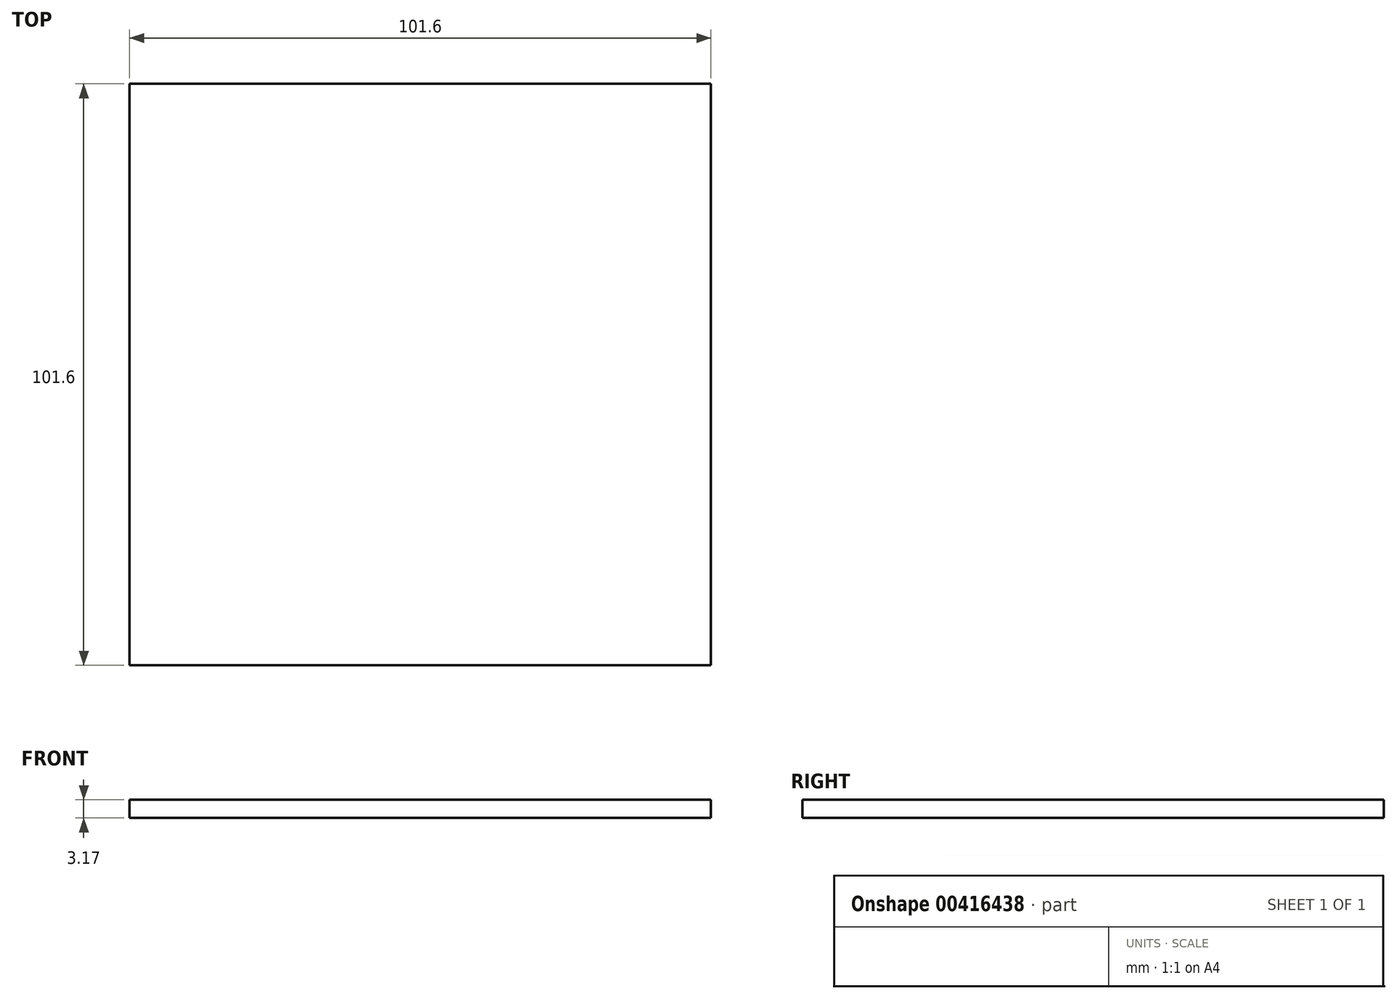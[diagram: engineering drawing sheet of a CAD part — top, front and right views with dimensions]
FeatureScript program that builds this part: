
annotation { "Feature Type Name" : "Feature", "Feature Type Description" : "" }
export const myFeature = defineFeature(function(context is Context, id is Id, definition is map)
    precondition{}
    {
        {
            var Q0;
            Q0=qCreatedBy(makeId("Top.planeOp"),FACE);
            var sketch = newSketch(context, id + "F0", { "sketchPlane" : qUnion([Q0])});
            skLineSegment(sketch, "E0.bottom", {"start": v(50.8, 50.8) * mm, "end": v(-50.8, 50.8) * mm});
            skLineSegment(sketch, "E0.top", {"start": v(50.8, -50.8) * mm, "end": v(-50.8, -50.8) * mm});
            skLineSegment(sketch, "E0.left", {"start": v(50.8, 50.8) * mm, "end": v(50.8, -50.8) * mm});
            skLineSegment(sketch, "E0.right", {"start": v(-50.8, 50.8) * mm, "end": v(-50.8, -50.8) * mm});
            skPoint(sketch, "E0.middle", {"position": v(0, 0) * mm});
            skSolve(sketch);
        }
        {
            var Q0;
            Q0=makeQuery(id+"F0.imprint","IMPRINT",FACE,{"disambiguationData":[TD([[makeQuery(id+"F0.imprint","IMPRINT",EDGE,{"derivedFrom":sQuery(id+"F0.wireOp",EDGE,"E0.bottom")}),1.0]])]});
            extrude(context, id + "F1", {"entities" : qUnion([Q0]), "depth" : 3.17 * mm});
        }
    });
